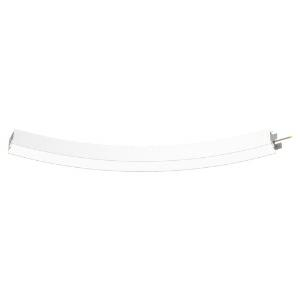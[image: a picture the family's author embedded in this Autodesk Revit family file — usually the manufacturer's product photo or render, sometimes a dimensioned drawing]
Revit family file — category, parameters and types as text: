
# Revit family: super-g_slim_super_g_slim_3000_45deg_ab_ps_led__24w_3160lm_3000k_cri_80_350-1420_c89e
name_source: partatom
category: Leuchten
revit_build: Autodesk Revit 2016 (Build: 20190508_0715(x64)
units: mm (PartAtom-declared; Revit-internal decimal feet)

## family parameters
Basisbauteil = Fläche
Beim Laden mit Abzugskörper schneiden = Nein
Bemaßung runder Anschluss = Durchmesser verwenden
Gemeinsam genutzt = Nein
Lichtquelle = Nein
Raumberechnungspunkt = Nein
Teiletyp = Normal

## types (1)
- 350-1420-D01 (1 x LED, 480 lm, 3000K)
    Approval mark = CE
    Beschreibung = The insert consists of aluminum-extruded profile. Charming SOFT-EDGE design ensure unparalleled styling. The ballast is integrated and allows for an operation with 220-240V (50/60Hz). SUPER-G SLIM (# 350-1420) ist not dimmable (on/off).
    CIE Flux Codes = 48 79 96 100 71
    Color Rendering = 1B/80…89
    Color Temperature = 3000K
    Height = 90 mm
    Hersteller = Prolicht
    Lamp Light Flux = 480 lm
    Lamp count = 1
    Lampe = 1 x LED
    Length = 144 mm
    Luminous efficacy = 103 lm/W
    ModVariant = Nein
    Modell = 350-1420
    Mounting Place = Ceiling
    Mounting Type = Surface mounted
    Number of Poles = 1
    OnlyDefault = Ja
    Power Factor = 1
    Product Name = SUPER-G SLIM__SUPER G SLIM 3000/45° AB PS LED: 24W 3160lm 3000K CRI:80
    Product group = Surface profile systems
    ProductGroupID = 335
    Protection Class = Protection class I
    Protection Degree = IP 20
    RLX_Detail_Level = 1
    RlxData = <blob elided: 29989 chars, md5=98207c33>
    Scheinlast = 26 VA
    Socket = socket
    Standby Power = 0 W
    System Light Flux = 2723 lm
    System Power = 26 W
    Typenbild = 350-1420.jpg
    URL = http://relux.com
    VarID = 350-1420-d01
    Voltage = 0 V
    Vorgabe-Ansicht = 1800 mm
    Weight = 0.00 kg
    Width = 65 mm

## geometry (parser evidence)
native form markers: Blend x4, Sweep x33
no freeform markers — native parametric forms only
